# Revit family: Deckel_Bogen_45_Russia
name_source: partatom
category: Generic Models
revit_build: Autodesk Revit 2015 (Build: 20140606_1530(x64)
units: mm (PartAtom-declared; Revit-internal decimal feet)

## types (7) — shared parameters
Manufacturer = OBO Bettermann
Material = Steel, Galvanized
URL = http://www.obo-bettermann.com

## per-type parameters (varying)
| type | A | B | GTIN | Manufacturer Art. No. |
| DFB 45 100 FS RU | 225 mm  [stored 0.738189 ft] | 92 mm  [stored 0.301837 ft] | 4012196606351 | 7128931 |
| DFB 45 150 FS RU | 263 mm  [stored 0.862861 ft] | 138 mm  [stored 0.452756 ft] | 4012196649464 | 7128932 |
| DFB 45 200 FS RU | 301 mm  [stored 0.987533 ft] | 185 mm  [stored 0.606955 ft] | 4012196606368 | 7128933 |
| DFB 45 300 FS RU | 378 mm  [stored 1.24016 ft] | 277 mm  [stored 0.908793 ft] | 4012196606375 | 7128935 |
| DFB 45 400 FS RU | 454 mm  [stored 1.4895 ft] | 369 mm | 4012196626380 | 7128937 |
| DFB 45 500 FS RU | 531 mm  [stored 1.74213 ft] | 462 mm  [stored 1.51575 ft] | 4012196626397 | 7128939 |
| DFB 45 600 FS RU | 607 mm  [stored 1.99147 ft] | 554 mm  [stored 1.81759 ft] | 4012196626403 | 7128941 |

note: column(s) folded — value = type name in every type: Article Type

note: [stored X ft] marks values corroborated as IEEE doubles in the binary element streams (Revit-internal decimal feet)

## geometry (parser evidence)
native form markers: Sweep x2
no freeform markers — native parametric forms only
